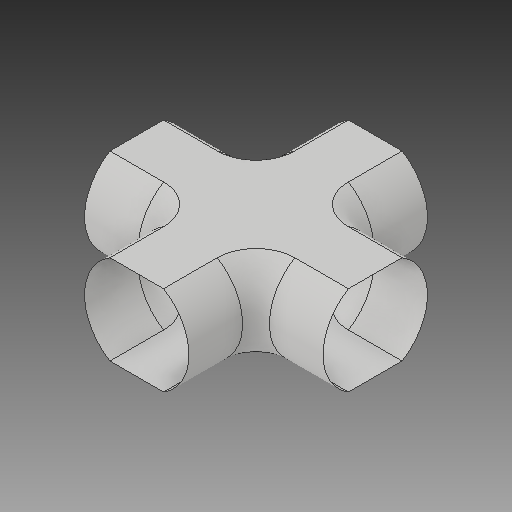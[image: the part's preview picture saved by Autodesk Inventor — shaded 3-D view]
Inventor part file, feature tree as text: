
AUTODESK INVENTOR PART (.ipt)
format: ipt  version: 2017 (Build 210142000, 142)  size: 229,376 bytes
history: native  units: in
note: dims shown in document units (in); Inventor stores cm internally (conversion verified against a paired STEP export)
features: sketch x4, extrude x3, mirror x3, plane x1, sweep x1, delete_face x1, other x1
ambient origin geometry x8: Origin, YZ Plane, XZ Plane, XY Plane, X Axis, Y Axis, Z Axis, Center Point
bodies: Body1 (feature_tree)
feature tree (14):
  extrude  "corridor eighth"  Depth=9.7746in TaperAngle=45.0deg
  plane  "Work Plane1"
  sketch  "Sketch17"  dims[d160=4.0in d168=10.3167in d169=10.3167in]
  sketch  "Sketch7"  dims[d0=6.6667in d2=9.7746in d5=-4.8873in d62=45.0deg d71=4.0in d72=0.0in]
  sweep  "curve"
  mirror  "mirror plane YZ"
  extrude  "corridor eighth complete"  Depth=10.3167in
  mirror  "Mirror half"
  mirror  "Mirrorfull"
  extrude  "hole fill in"  Depth=3.3333in
  delete_face  "Delete Face1"
  other  "corridor"
  sketch  "Sketch22"  dims[d170=10.3167in d171=10.3167in]
  sketch  "Sketch24"  dims[d196=4.0in d198=3.8873in d199=3.8873in d203=1.6458in d209=3.3333in d211=1.0in d212=0.0in d213=0.0in d214=4.0in d215=0.0in d216=4.0in d217=0.0in]
